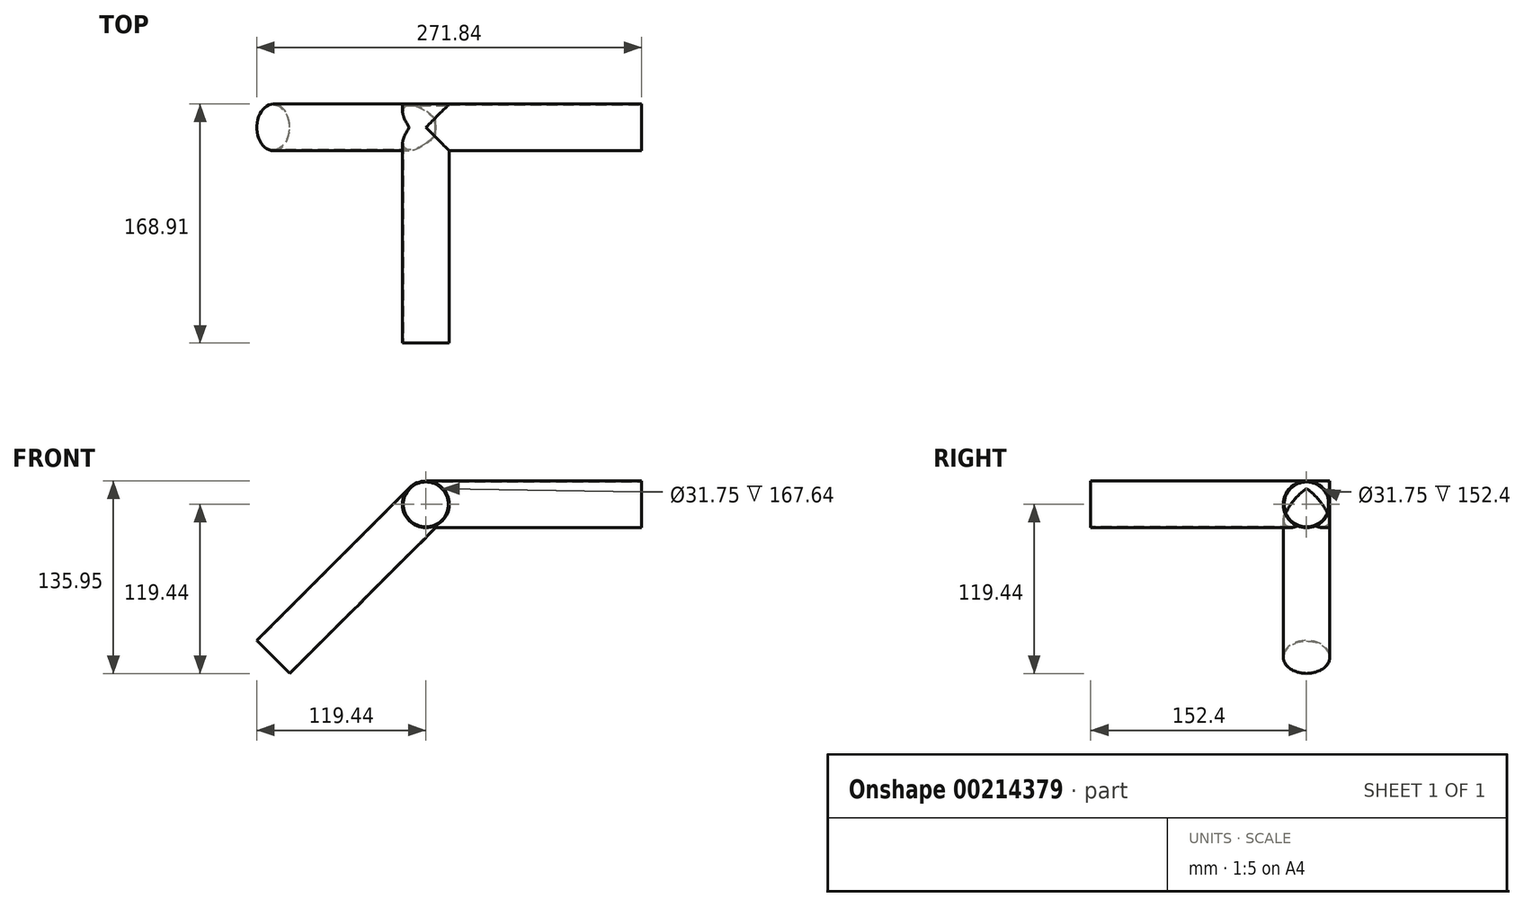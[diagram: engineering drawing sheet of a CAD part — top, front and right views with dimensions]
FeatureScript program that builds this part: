
annotation { "Feature Type Name" : "Feature", "Feature Type Description" : "" }
export const myFeature = defineFeature(function(context is Context, id is Id, definition is map)
    precondition{}
    {
        {
            var Q0;
            Q0=qCreatedBy(makeId("Front.planeOp"),FACE);
            var sketch = newSketch(context, id + "F0", { "sketchPlane" : qUnion([Q0])});
            skCircle(sketch, "E0", {"center": v(0, 0) * mm, "radius": 16.51 * mm});
            skSolve(sketch);
        }
        {
            var Q0;
            Q0=qSketchRegion(id+"F0",true);
            extrude(context, id + "F1", {"entities" : qUnion([Q0]), "depth" : 152.4 * mm, "hasSecondDirection" : true, "secondDirectionOppositeDirection" : true, "secondDirectionDepth" : 152.4 * mm});
        }
        {
            var Q0;
            Q0=qCreatedBy(makeId("Right.planeOp"),FACE);
            var sketch = newSketch(context, id + "F2", { "sketchPlane" : qUnion([Q0])});
            skCircle(sketch, "E1", {"center": v(0, 0) * mm, "radius": 16.51 * mm});
            skSolve(sketch);
        }
        {
            var Q0;
            Q0=qSketchRegion(id+"F2",true);
            extrude(context, id + "F3", {"entities" : qUnion([Q0]), "operationType" : NewBodyOperationType.ADD, "depth" : 152.4 * mm});
        }
        {
            var Q0;
            Q0=qCreatedBy(makeId("Right.planeOp"),FACE);
            var Q1;
            Q1=qCreatedBy(makeId("Top.planeOp"),FACE);
            cPlane(context, id + "F4", {"entities" : qUnion([Q0, Q1]), "cplaneType" : CPlaneType.MID_PLANE, "offset" : 25.4 * mm, "flipAlignment" : true, "width" : 152.4 * mm, "height" : 152.4 * mm});
        }
        {
            var Q0;
            Q0=qCreatedBy(id+"F4.planeOp",FACE);
            var sketch = newSketch(context, id + "F5", { "sketchPlane" : qUnion([Q0])});
            skCircle(sketch, "E2", {"center": v(0, 0) * mm, "radius": 16.51 * mm});
            skSolve(sketch);
        }
        {
            var Q0;
            Q0=qSketchRegion(id+"F5",true);
            extrude(context, id + "F6", {"entities" : qUnion([Q0]), "operationType" : NewBodyOperationType.ADD, "oppositeDirection" : true, "depth" : 152.4 * mm});
        }
        {
            var Q0;
            Q0=makeQuery(id+"F1.opExtrude","CAP_FACE",FACE,{"disambiguationData":[OSD([sQuery(id+"F0.wireOp",EDGE,"E0")])],"isStart":false});
            var sketch = newSketch(context, id + "F7", { "sketchPlane" : qUnion([Q0])});
            skCircle(sketch, "E3", {"center": v(0, 0) * mm, "radius": 15.88 * mm});
            skSolve(sketch);
        }
        {
            var Q0;
            Q0=qSketchRegion(id+"F7",true);
            extrude(context, id + "F8", {"entities" : qUnion([Q0]), "operationType" : NewBodyOperationType.REMOVE, "endBound" : BoundingType.THROUGH_ALL, "oppositeDirection" : true, "depth" : 25.4 * mm});
        }
        {
            var Q0;
            Q0=makeQuery(id+"F3.opExtrude","CAP_FACE",FACE,{"disambiguationData":[OSD([sQuery(id+"F2.wireOp",EDGE,"E1")])],"isStart":false});
            var sketch = newSketch(context, id + "F9", { "sketchPlane" : qUnion([Q0])});
            skCircle(sketch, "E4", {"center": v(0, 0) * mm, "radius": 15.88 * mm});
            skSolve(sketch);
        }
        {
            var Q0;
            Q0=qSketchRegion(id+"F9",true);
            var Q1;
            Q1=makeQuery(id+"F8.boolean.opBoolean","COPY",FACE,{"derivedFrom":makeQuery(id+"F8.opExtrude","SWEPT_FACE",FACE,{"disambiguationData":[OSD([sQuery(id+"F7.wireOp",EDGE,"E3")])]})});
            extrude(context, id + "F10", {"entities" : qUnion([Q0]), "operationType" : NewBodyOperationType.REMOVE, "endBound" : BoundingType.UP_TO_SURFACE, "oppositeDirection" : true, "endBoundEntityFace" : qUnion([Q1]), "depth" : 25.4 * mm});
        }
        {
            var Q0;
            Q0=makeQuery(id+"F6.opExtrude","CAP_FACE",FACE,{"disambiguationData":[OSD([sQuery(id+"F5.wireOp",EDGE,"E2")])],"isStart":false});
            var sketch = newSketch(context, id + "F11", { "sketchPlane" : qUnion([Q0])});
            skCircle(sketch, "E5", {"center": v(0, 0) * mm, "radius": 15.88 * mm});
            skSolve(sketch);
        }
        {
            var Q0;
            Q0=qSketchRegion(id+"F11",true);
            var Q1;
            Q1=makeQuery(id+"F8.boolean.opBoolean","COPY",FACE,{"derivedFrom":makeQuery(id+"F8.opExtrude","SWEPT_FACE",FACE,{"disambiguationData":[OSD([sQuery(id+"F7.wireOp",EDGE,"E3")])]})});
            extrude(context, id + "F12", {"entities" : qUnion([Q0]), "operationType" : NewBodyOperationType.REMOVE, "endBound" : BoundingType.UP_TO_SURFACE, "oppositeDirection" : true, "endBoundEntityFace" : qUnion([Q1]), "depth" : 25.4 * mm});
        }
        {
            var Q0;
            Q0=makeQuery(id+"F1.opExtrude","CAP_FACE",FACE,{"disambiguationData":[OSD([sQuery(id+"F0.wireOp",EDGE,"E0")])],"isStart":true});
            var sketch = newSketch(context, id + "F13", { "sketchPlane" : qUnion([Q0])});
            skCircle(sketch, "E6", {"center": v(0, 0) * mm, "radius": 16.51 * mm});
            skSolve(sketch);
        }
        {
            var Q0;
            Q0=qSketchRegion(id+"F13",true);
            extrude(context, id + "F14", {"entities" : qUnion([Q0]), "operationType" : NewBodyOperationType.REMOVE, "oppositeDirection" : true, "depth" : 135.89 * mm});
        }
        {
            var Q0;
            Q0=makeQuery(id+"F14.boolean.opBoolean","COPY",FACE,{"derivedFrom":makeQuery(id+"F14.opExtrude","CAP_FACE",FACE,{"disambiguationData":[OSD([sQuery(id+"F13.wireOp",EDGE,"E6")])],"isStart":false})});
            var sketch = newSketch(context, id + "F15", { "sketchPlane" : qUnion([Q0])});
            skCircle(sketch, "E7", {"center": v(0, 0) * mm, "radius": 16.51 * mm});
            skSolve(sketch);
        }
        {
            var Q0;
            Q0=qSketchRegion(id+"F15",true);
            extrude(context, id + "F16", {"entities" : qUnion([Q0]), "operationType" : NewBodyOperationType.ADD, "oppositeDirection" : true, "depth" : 1.27 * mm});
        }
    });
